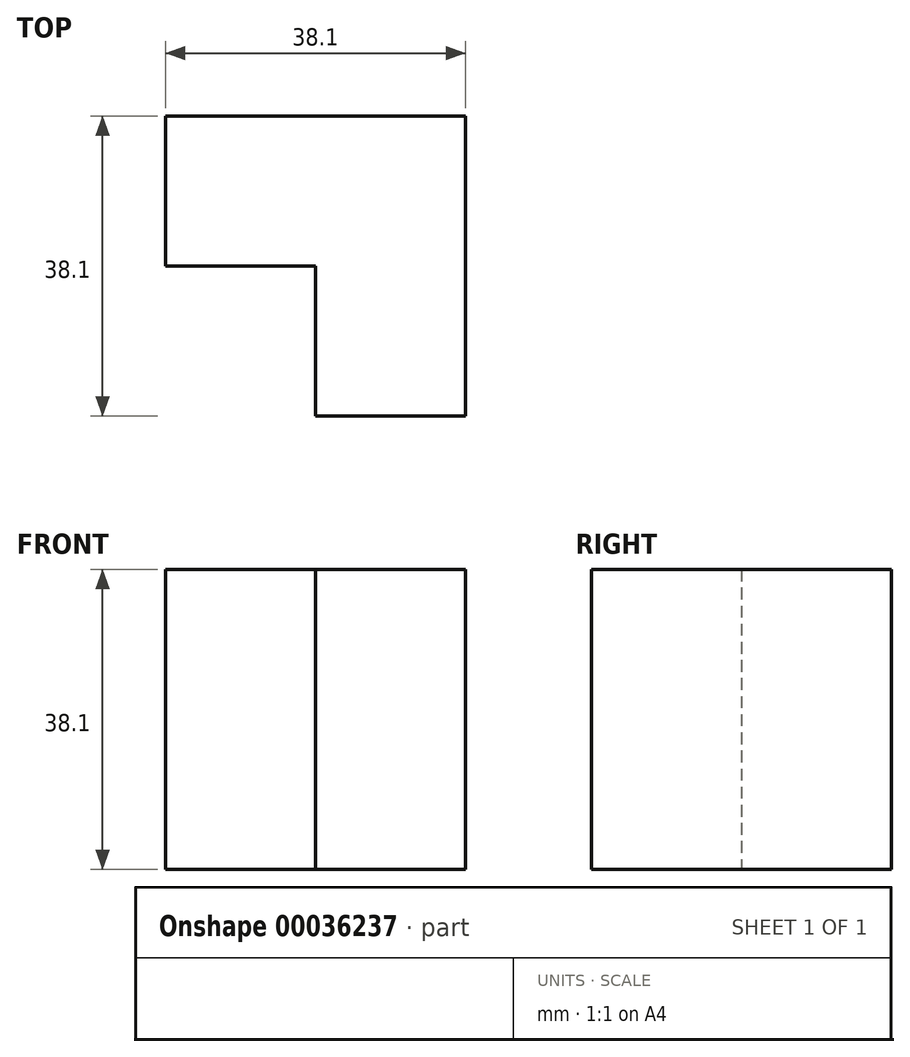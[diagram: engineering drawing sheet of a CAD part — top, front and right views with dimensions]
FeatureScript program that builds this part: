
annotation { "Feature Type Name" : "Feature", "Feature Type Description" : "" }
export const myFeature = defineFeature(function(context is Context, id is Id, definition is map)
    precondition{}
    {
        {
            var Q0;
            Q0=qCreatedBy(makeId("Top.planeOp"),FACE);
            var sketch = newSketch(context, id + "F0", { "sketchPlane" : qUnion([Q0])});
            skLineSegment(sketch, "E0.bottom", {"start": v(0, 0) * mm, "end": v(-38.1, 0) * mm});
            skLineSegment(sketch, "E0.top", {"start": v(0, -19.05) * mm, "end": v(-38.1, -19.05) * mm});
            skLineSegment(sketch, "E0.left", {"start": v(0, 0) * mm, "end": v(0, -19.05) * mm});
            skLineSegment(sketch, "E0.right", {"start": v(-38.1, 0) * mm, "end": v(-38.1, -19.05) * mm});
            skSolve(sketch);
        }
        {
            var Q0;
            Q0=makeQuery(id+"F0.imprint","IMPRINT",FACE,{"disambiguationData":[TD([[makeQuery(id+"F0.imprint","IMPRINT",EDGE,{"derivedFrom":sQuery(id+"F0.wireOp",EDGE,"E0.bottom")}),1.0]])]});
            extrude(context, id + "F1", {"entities" : qUnion([Q0]), "oppositeDirection" : true, "depth" : 19.05 * mm});
        }
        {
            var Q0;
            Q0=makeQuery(id+"F1.opExtrude","SWEPT_FACE",FACE,{"disambiguationData":[OSD([sQuery(id+"F0.wireOp",EDGE,"E0.top")])]});
            var sketch = newSketch(context, id + "F2", { "sketchPlane" : qUnion([Q0])});
            skLineSegment(sketch, "E1.bottom", {"start": v(0, 0) * mm, "end": v(-19.05, 0) * mm});
            skLineSegment(sketch, "E1.top", {"start": v(0, -19.05) * mm, "end": v(-19.05, -19.05) * mm});
            skLineSegment(sketch, "E1.left", {"start": v(0, 0) * mm, "end": v(0, -19.05) * mm});
            skLineSegment(sketch, "E1.right", {"start": v(-19.05, 0) * mm, "end": v(-19.05, -19.05) * mm});
            skSolve(sketch);
        }
        {
            var Q0;
            Q0 = qSketchRegion(id + "F2", true);
            extrude(context, id + "F3", {"entities" : qUnion([Q0]), "operationType" : NewBodyOperationType.ADD, "depth" : 19.05 * mm});
        }
        {
            var Q0;
            Q0=makeQuery(id+"F3.boolean.opBoolean","MERGE",FACE,{"derivedFrom":[makeQuery(id+"F1.opExtrude","CAP_FACE",FACE,{"disambiguationData":[OSD([sQuery(id+"F0.wireOp",EDGE,"E0.bottom"),sQuery(id+"F0.wireOp",EDGE,"E0.top"),sQuery(id+"F0.wireOp",EDGE,"E0.left"),sQuery(id+"F0.wireOp",EDGE,"E0.right")])],"isStart":false}),makeQuery(id+"F3.opExtrude","SWEPT_FACE",FACE,{"disambiguationData":[OSD([sQuery(id+"F2.wireOp",EDGE,"E1.top")])]})]});
            extrude(context, id + "F4", {"entities" : qUnion([Q0]), "operationType" : NewBodyOperationType.ADD, "depth" : 19.05 * mm});
        }
    });
